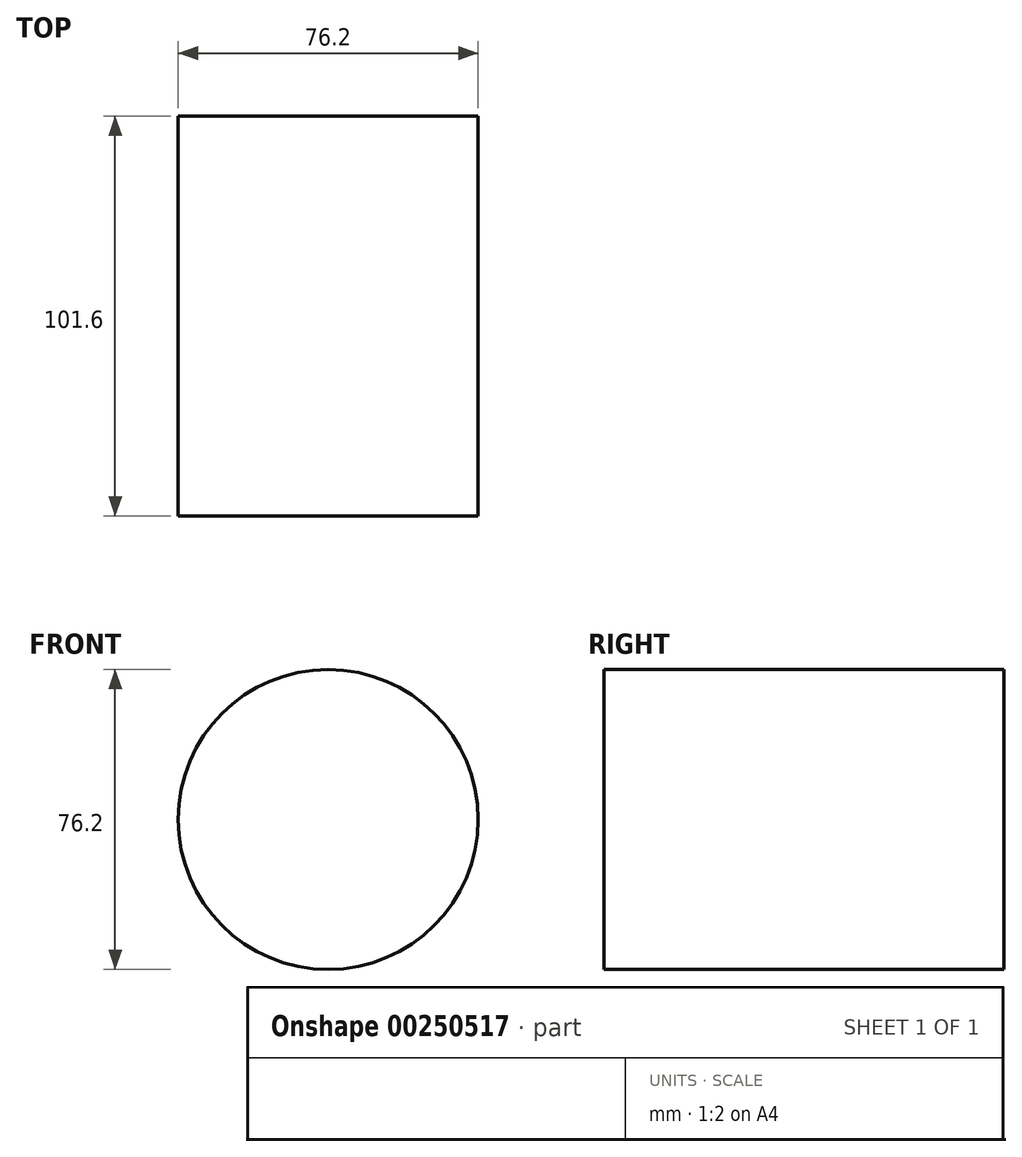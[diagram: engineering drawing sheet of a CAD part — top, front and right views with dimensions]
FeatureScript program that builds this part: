
annotation { "Feature Type Name" : "Feature", "Feature Type Description" : "" }
export const myFeature = defineFeature(function(context is Context, id is Id, definition is map)
    precondition{}
    {
        {
            var Q0;
            Q0=qCreatedBy(makeId("Front.planeOp"),FACE);
            var sketch = newSketch(context, id + "F0", { "sketchPlane" : qUnion([Q0])});
            skCircle(sketch, "E0", {"center": v(0, 0) * mm, "radius": 38.1 * mm});
            skCircle(sketch, "E1", {"center": v(0, 0) * mm, "radius": 19.05 * mm});
            skSolve(sketch);
        }
        {
            var Q0;
            Q0=makeQuery(id+"F0.imprint","IMPRINT",FACE,{"disambiguationData":[TD([[makeQuery(id+"F0.imprint","IMPRINT",EDGE,{"derivedFrom":sQuery(id+"F0.wireOp",EDGE,"E1")}),1.0]])]});
            var Q1;
            Q1=makeQuery(id+"F0.imprint","IMPRINT",FACE,{"disambiguationData":[TD([[makeQuery(id+"F0.imprint","IMPRINT",EDGE,{"derivedFrom":sQuery(id+"F0.wireOp",EDGE,"E0")}),1.0]])]});
            extrude(context, id + "F1", {"entities" : qUnion([Q0, Q1]), "endBound" : BoundingType.SYMMETRIC, "depth" : 101.6 * mm});
        }
        {
            var Q0;
            Q0=sQuery(id+"F0.wireOp",EDGE,"E1");
            extrude(context, id + "F2", {"bodyType" : ToolBodyType.SURFACE, "surfaceEntities" : qUnion([Q0]), "endBound" : BoundingType.SYMMETRIC, "depth" : 203.2 * mm});
        }
    });
